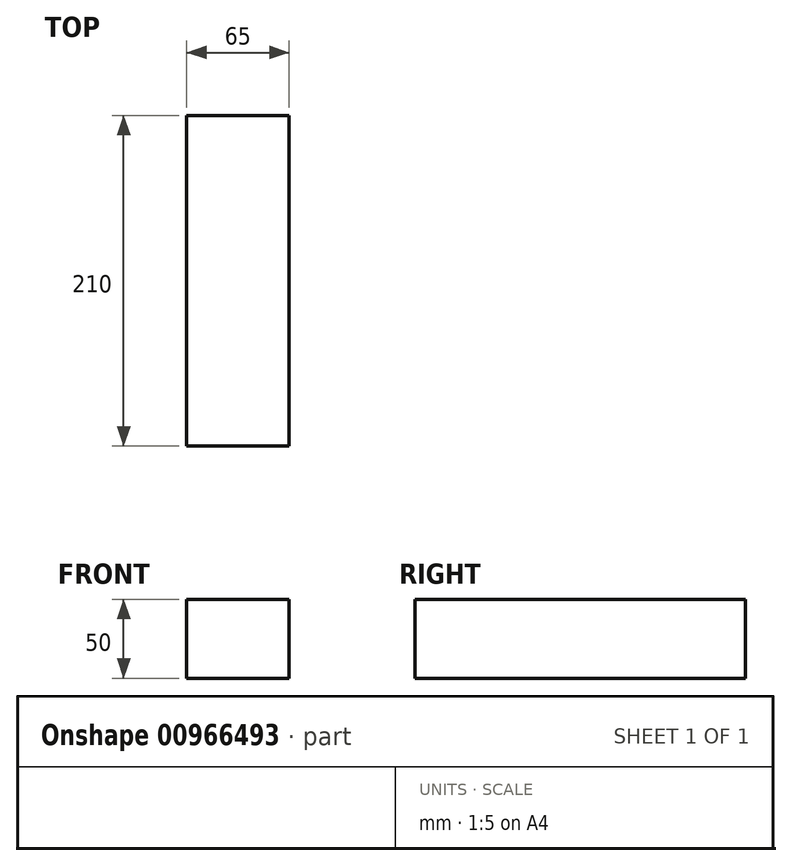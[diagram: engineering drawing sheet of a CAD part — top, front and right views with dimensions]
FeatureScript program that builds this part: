
annotation { "Feature Type Name" : "Feature", "Feature Type Description" : "" }
export const myFeature = defineFeature(function(context is Context, id is Id, definition is map)
    precondition{}
    {
        {
            var Q0;
            Q0=qCreatedBy(makeId("Front.planeOp"),FACE);
            var sketch = newSketch(context, id + "F0", { "sketchPlane" : qUnion([Q0])});
            skLineSegment(sketch, "E0.bottom", {"start": v(32.5, -25) * mm, "end": v(-32.5, -25) * mm});
            skLineSegment(sketch, "E0.top", {"start": v(32.5, 25) * mm, "end": v(-32.5, 25) * mm});
            skLineSegment(sketch, "E0.left", {"start": v(32.5, -25) * mm, "end": v(32.5, 25) * mm});
            skLineSegment(sketch, "E0.right", {"start": v(-32.5, -25) * mm, "end": v(-32.5, 25) * mm});
            skPoint(sketch, "E0.middle", {"position": v(0, 0) * mm});
            skSolve(sketch);
        }
        {
            var Q0;
            Q0=makeQuery(id+"F0.imprint","IMPRINT",FACE,{"disambiguationData":[TD([[makeQuery(id+"F0.imprint","IMPRINT",EDGE,{"derivedFrom":sQuery(id+"F0.wireOp",EDGE,"E0.bottom")}),-1.0]])]});
            extrude(context, id + "F1", {"entities" : qUnion([Q0]), "oppositeDirection" : true, "depth" : 210 * mm, "offsetDistance" : 25 * mm});
        }
    });
